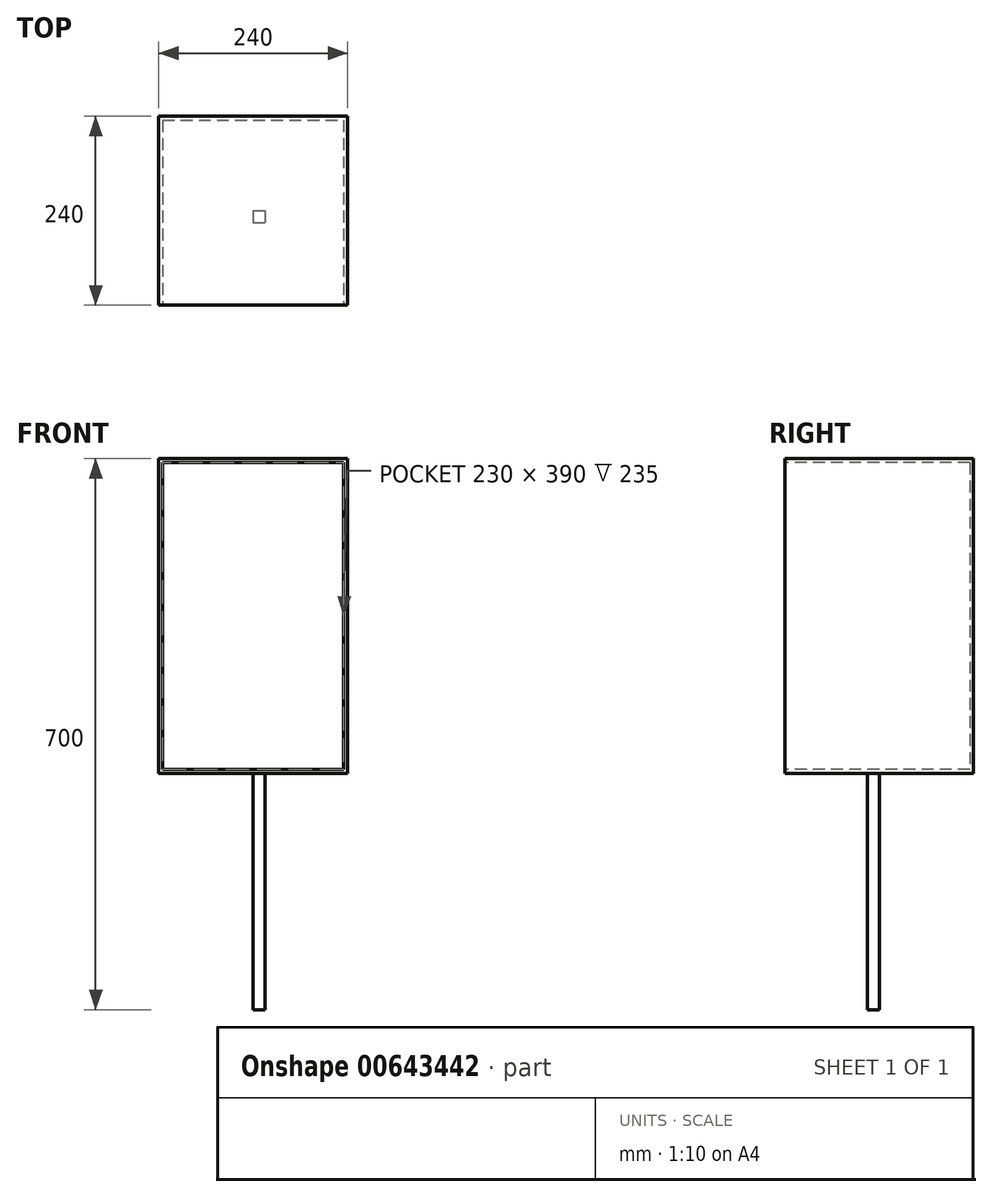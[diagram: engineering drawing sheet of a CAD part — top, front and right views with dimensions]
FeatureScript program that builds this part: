
annotation { "Feature Type Name" : "Feature", "Feature Type Description" : "" }
export const myFeature = defineFeature(function(context is Context, id is Id, definition is map)
    precondition{}
    {
        {
            var Q0;
            Q0=qCreatedBy(makeId("Front.planeOp"),FACE);
            var sketch = newSketch(context, id + "F0", { "sketchPlane" : qUnion([Q0])});
            skLineSegment(sketch, "E0.bottom", {"start": v(-240, 400) * mm, "end": v(0, 400) * mm});
            skLineSegment(sketch, "E0.top", {"start": v(-240, 0) * mm, "end": v(0, 0) * mm});
            skLineSegment(sketch, "E0.left", {"start": v(-240, 400) * mm, "end": v(-240, 0) * mm});
            skLineSegment(sketch, "E0.right", {"start": v(0, 400) * mm, "end": v(0, 0) * mm});
            skSolve(sketch);
        }
        {
            var Q0;
            Q0=makeQuery(id+"F0.imprint","IMPRINT",FACE,{"disambiguationData":[TD([[makeQuery(id+"F0.imprint","IMPRINT",EDGE,{"derivedFrom":sQuery(id+"F0.wireOp",EDGE,"E0.bottom")}),-1.0]])]});
            extrude(context, id + "F1", {"entities" : qUnion([Q0]), "oppositeDirection" : true, "depth" : 240 * mm, "offsetDistance" : 25 * mm});
        }
        {
            var Q0;
            Q0=makeQuery(id+"F1.opExtrude","CAP_FACE",FACE,{"disambiguationData":[OSD([sQuery(id+"F0.wireOp",EDGE,"E0.bottom"),sQuery(id+"F0.wireOp",EDGE,"E0.top"),sQuery(id+"F0.wireOp",EDGE,"E0.left"),sQuery(id+"F0.wireOp",EDGE,"E0.right")])],"isStart":true});
            shell(context, id + "F2", {"entities" : qUnion([Q0]), "thickness" : 5 * mm});
        }
        {
            var Q0;
            Q0=qCreatedBy(makeId("Top.planeOp"),FACE);
            var sketch = newSketch(context, id + "F3", { "sketchPlane" : qUnion([Q0])});
            skLineSegment(sketch, "E1.bottom", {"start": v(-120, 120) * mm, "end": v(-105, 120) * mm});
            skLineSegment(sketch, "E1.top", {"start": v(-120, 105) * mm, "end": v(-105, 105) * mm});
            skLineSegment(sketch, "E1.left", {"start": v(-120, 120) * mm, "end": v(-120, 105) * mm});
            skLineSegment(sketch, "E1.right", {"start": v(-105, 120) * mm, "end": v(-105, 105) * mm});
            skSolve(sketch);
        }
        {
            var Q0;
            Q0=makeQuery(id+"F3.imprint","IMPRINT",FACE,{"disambiguationData":[TD([[makeQuery(id+"F3.imprint","IMPRINT",EDGE,{"derivedFrom":sQuery(id+"F3.wireOp",EDGE,"E1.bottom")}),-1.0]])]});
            extrude(context, id + "F4", {"entities" : qUnion([Q0]), "oppositeDirection" : true, "depth" : 300 * mm, "offsetDistance" : 25 * mm});
        }
    });
